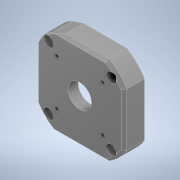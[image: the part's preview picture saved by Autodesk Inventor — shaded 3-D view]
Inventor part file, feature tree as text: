
AUTODESK INVENTOR PART (.ipt)
format: ipt  version: 2022 (Build 260153000, 153)  size: 200,704 bytes
history: mixed  units: in
note: dims shown in document units (in); Inventor stores cm internally (conversion verified against a paired STEP export)
features: extrude x3, sketch x3, chamfer x2, fillet x1, imported_body x1
ambient origin geometry x8: Origin, YZ Plane, XZ Plane, XY Plane, X Axis, Y Axis, Z Axis, Center Point
bodies: Solid1 (imported_parasolid)
feature tree (10):
  extrude  "Extrusion1"  Depth=0.3937in TaperAngle=0.0deg
  extrude  "Extrusion2"  Depth=0.3937in TaperAngle=0.0deg
  extrude  "Extrusion3"  TaperAngle=0.0deg  [1 undecoded]
  chamfer  "Chamfer1"  Distance=0.2662in Angle=45.0deg
  fillet  "Fillet1"  Radius=0.5787in
  sketch  "Sketch1"  dims[d0=0.1102in d1=0.3937in d2=0.0in]
  sketch  "Sketch2"  dims[d3=0.5906in d4=0.3937in d5=0.0in]
  sketch  "Sketch3"  dims[d6=0.6299in d7=0.0in d8=0.0in d9=0.2662in d10=0.0787in d11=45.0deg d12=0.5787in]
  chamfer  "Chamfer2"  [1 undecoded]
  imported_body  NMx_Import_Brep_tag  [imported B-rep: ~5 faces, bbox_mm=None]
note: 2 required parameter values undecoded (feature->parameter linkage not recoverable at this tier; creation-order binding heuristic only, values carry confidence <= 0.55)
